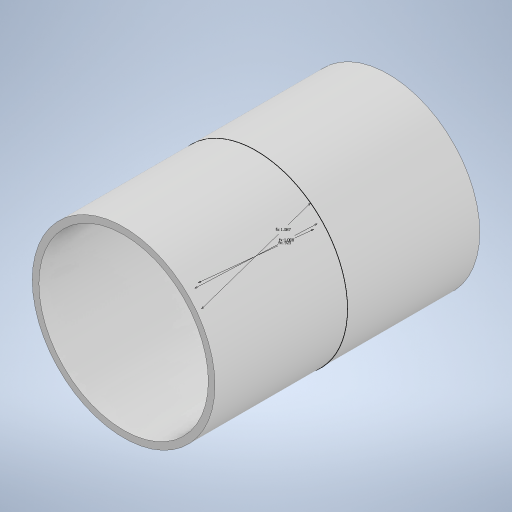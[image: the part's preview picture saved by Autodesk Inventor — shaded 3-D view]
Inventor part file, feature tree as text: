
AUTODESK INVENTOR PART (.ipt)
format: ipt  version: 2024 (Build 280153000, 153)  size: 221,184 bytes
history: native  units: in
note: dims shown in document units (in); Inventor stores cm internally (conversion verified against a paired STEP export)
features: extrude x2, sketch x1
ambient origin geometry x8: Origin, YZ Plane, XZ Plane, XY Plane, X Axis, Y Axis, Z Axis, Center Point
bodies: Solid1 (feature_tree)
feature tree (3):
  sketch  "Sketch1"  dims[d0=0.9252in d1=1.0079in d2=1.0866in d3=0.0394in d4=0.0in d5=0.7874in d6=0.7874in d7=0.0in d8=0.0in]
  extrude  "Extrusion1"  Depth=0.7874in
  extrude  "Extrusion2"  Depth=0.7874in
